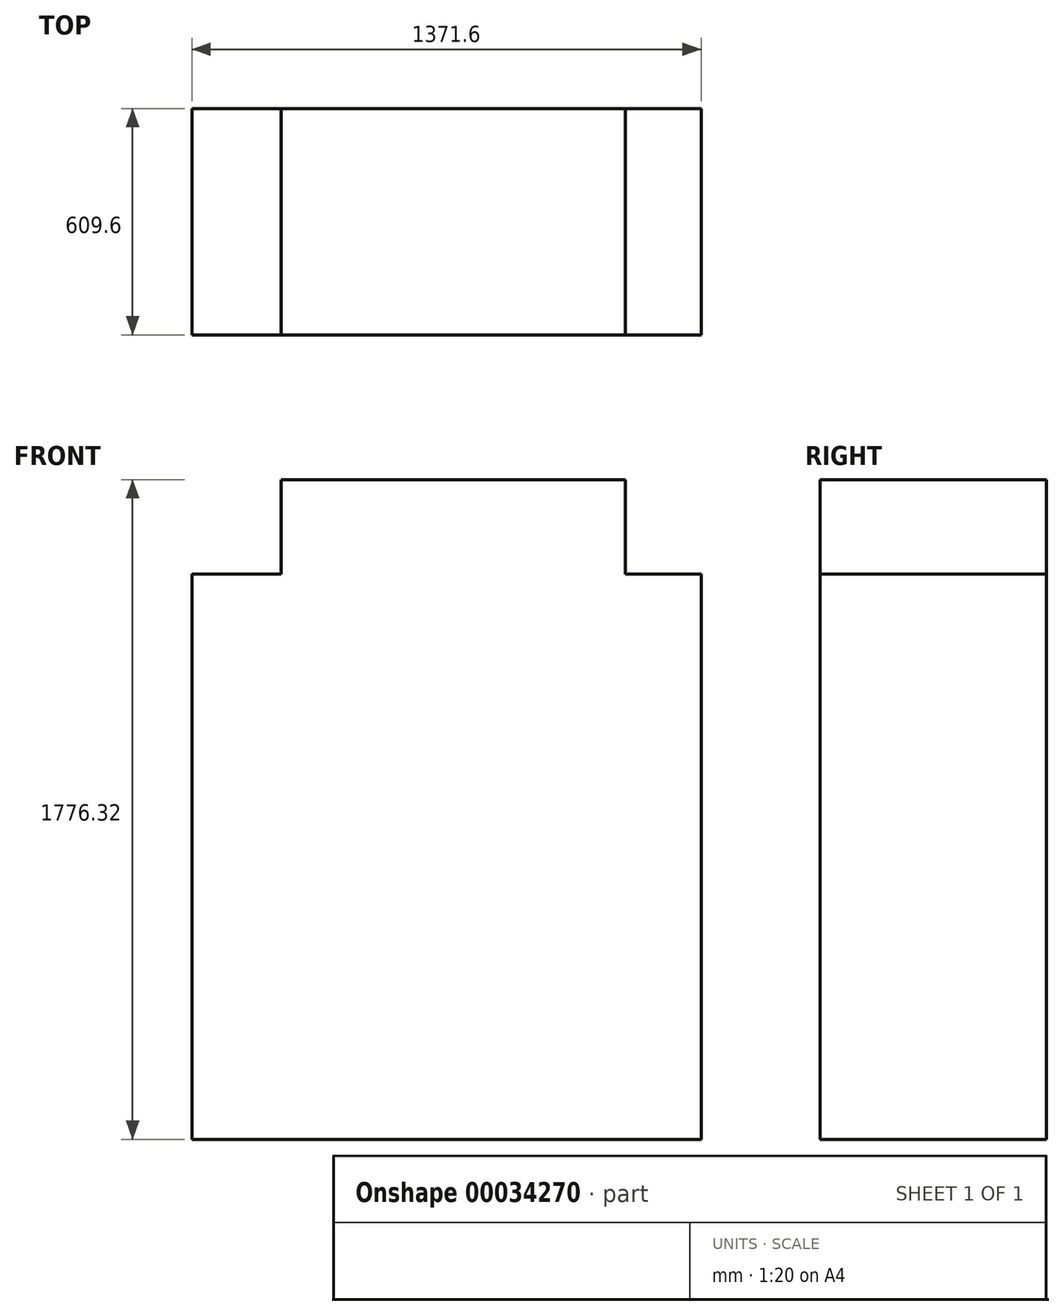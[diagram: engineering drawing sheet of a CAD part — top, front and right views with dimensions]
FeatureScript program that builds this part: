
annotation { "Feature Type Name" : "Feature", "Feature Type Description" : "" }
export const myFeature = defineFeature(function(context is Context, id is Id, definition is map)
    precondition{}
    {
        {
            var Q0;
            Q0=qCreatedBy(makeId("Top.planeOp"),FACE);
            var sketch = newSketch(context, id + "F0", { "sketchPlane" : qUnion([Q0])});
            skLineSegment(sketch, "E0.bottom", {"start": v(-631.71, 345.3) * mm, "end": v(739.89, 345.3) * mm});
            skLineSegment(sketch, "E0.top", {"start": v(-631.71, -264.3) * mm, "end": v(739.89, -264.3) * mm});
            skLineSegment(sketch, "E0.left", {"start": v(-631.71, 345.3) * mm, "end": v(-631.71, -264.3) * mm});
            skLineSegment(sketch, "E0.right", {"start": v(739.89, 345.3) * mm, "end": v(739.89, -264.3) * mm});
            skSolve(sketch);
        }
        {
            var Q0;
            Q0=makeQuery(id+"F0.imprint","IMPRINT",FACE,{"disambiguationData":[TD([[makeQuery(id+"F0.imprint","IMPRINT",EDGE,{"derivedFrom":sQuery(id+"F0.wireOp",EDGE,"E0.bottom")}),-1.0]])]});
            extrude(context, id + "F1", {"entities" : qUnion([Q0]), "depth" : 254 * mm});
        }
        {
            var Q0;
            Q0=makeQuery(id+"F1.opExtrude","CAP_FACE",FACE,{"disambiguationData":[OSD([sQuery(id+"F0.wireOp",EDGE,"E0.bottom"),sQuery(id+"F0.wireOp",EDGE,"E0.top"),sQuery(id+"F0.wireOp",EDGE,"E0.left"),sQuery(id+"F0.wireOp",EDGE,"E0.right")])],"isStart":false});
            var sketch = newSketch(context, id + "F2", { "sketchPlane" : qUnion([Q0])});
            skLineSegment(sketch, "E1.bottom", {"start": v(-391.36, 345.3) * mm, "end": v(535.18, 345.3) * mm});
            skLineSegment(sketch, "E1.top", {"start": v(-391.36, -264.3) * mm, "end": v(535.18, -264.3) * mm});
            skLineSegment(sketch, "E1.left", {"start": v(-391.36, 345.3) * mm, "end": v(-391.36, -264.3) * mm});
            skLineSegment(sketch, "E1.right", {"start": v(535.18, 345.3) * mm, "end": v(535.18, -264.3) * mm});
            skSolve(sketch);
        }
        {
            var Q0;
            Q0=makeQuery(id+"F2.imprint","IMPRINT",FACE,{"disambiguationData":[TD([[makeQuery(id+"F2.imprint","IMPRINT",EDGE,{"derivedFrom":sQuery(id+"F2.wireOp",EDGE,"E1.bottom")}),-1.0]])]});
            var Q1;
            Q1=makeQuery(id+"F1.opExtrude","CAP_FACE",FACE,{"disambiguationData":[OSD([sQuery(id+"F0.wireOp",EDGE,"E0.bottom"),sQuery(id+"F0.wireOp",EDGE,"E0.top"),sQuery(id+"F0.wireOp",EDGE,"E0.left"),sQuery(id+"F0.wireOp",EDGE,"E0.right")])],"isStart":true});
            extrude(context, id + "F3", {"entities" : qUnion([Q0, Q1]), "operationType" : NewBodyOperationType.ADD, "endBound" : BoundingType.THROUGH_ALL, "depth" : 25.4 * mm});
        }
    });
